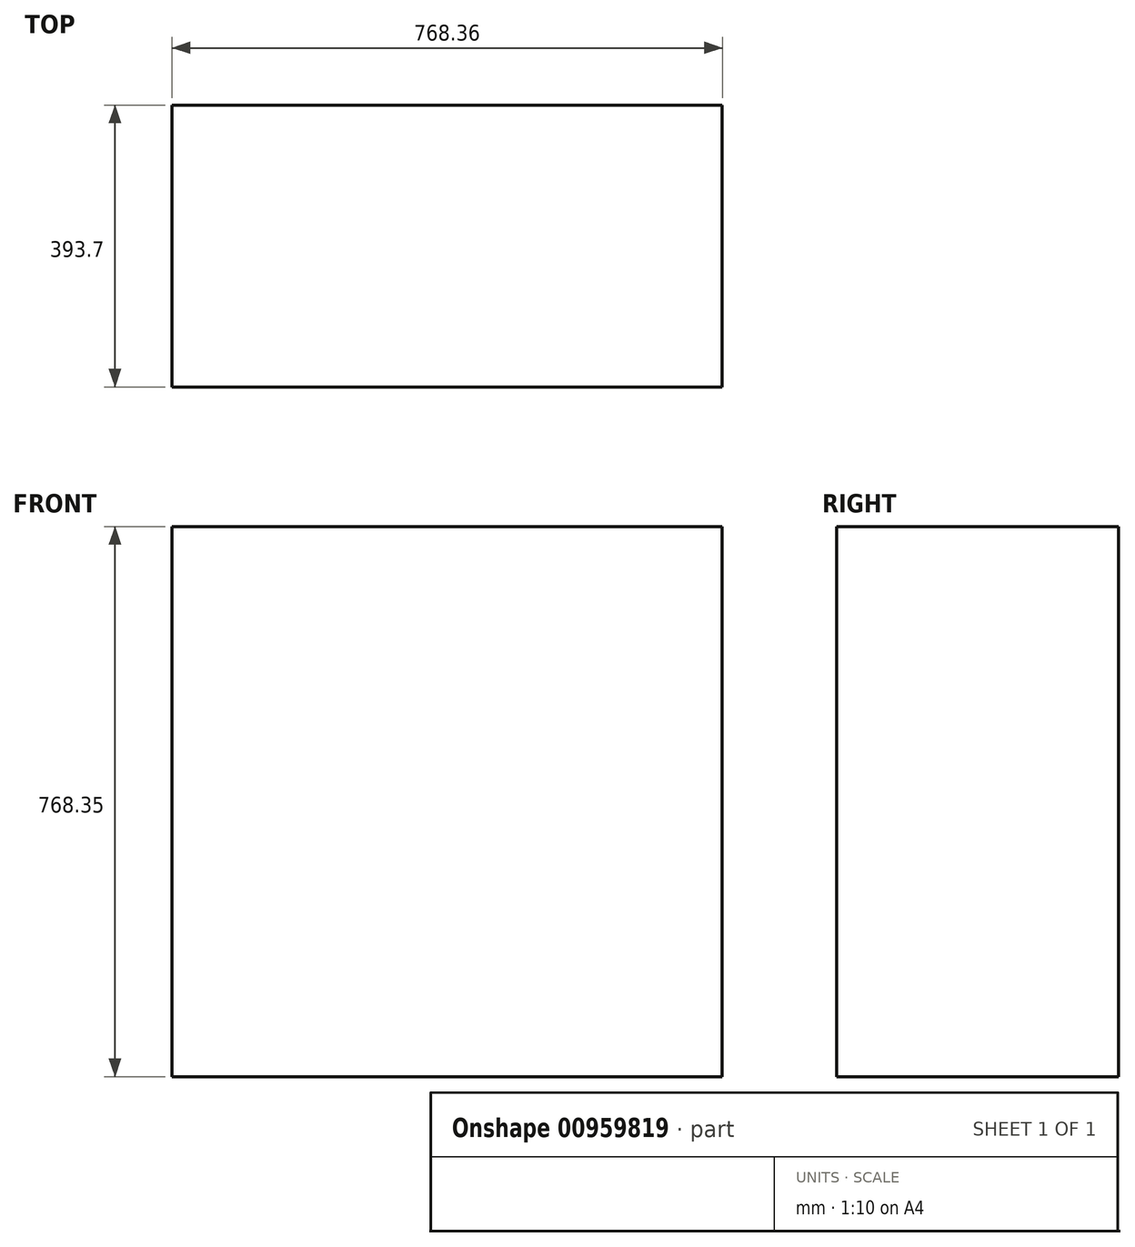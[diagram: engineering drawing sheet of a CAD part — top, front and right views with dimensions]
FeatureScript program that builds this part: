
annotation { "Feature Type Name" : "Feature", "Feature Type Description" : "" }
export const myFeature = defineFeature(function(context is Context, id is Id, definition is map)
    precondition{}
    {
        {
            var Q0;
            Q0=qCreatedBy(makeId("Top.planeOp"),FACE);
            var sketch = newSketch(context, id + "F0", { "sketchPlane" : qUnion([Q0])});
            skLineSegment(sketch, "E0.bottom", {"start": v(-384.18, 196.85) * mm, "end": v(384.18, 196.85) * mm});
            skLineSegment(sketch, "E0.top", {"start": v(-384.18, -196.85) * mm, "end": v(384.18, -196.85) * mm});
            skLineSegment(sketch, "E0.left", {"start": v(-384.18, 196.85) * mm, "end": v(-384.18, -196.85) * mm});
            skLineSegment(sketch, "E0.right", {"start": v(384.18, 196.85) * mm, "end": v(384.18, -196.85) * mm});
            skPoint(sketch, "E0.middle", {"position": v(0, 0) * mm});
            skSolve(sketch);
        }
        {
            var Q0;
            Q0=makeQuery(id+"F0.imprint","IMPRINT",FACE,{"disambiguationData":[TD([[makeQuery(id+"F0.imprint","IMPRINT",EDGE,{"derivedFrom":sQuery(id+"F0.wireOp",EDGE,"E0.bottom")}),-1.0]])]});
            extrude(context, id + "F1", {"entities" : qUnion([Q0]), "depth" : 768.35 * mm, "offsetDistance" : 25.4 * mm});
        }
    });
